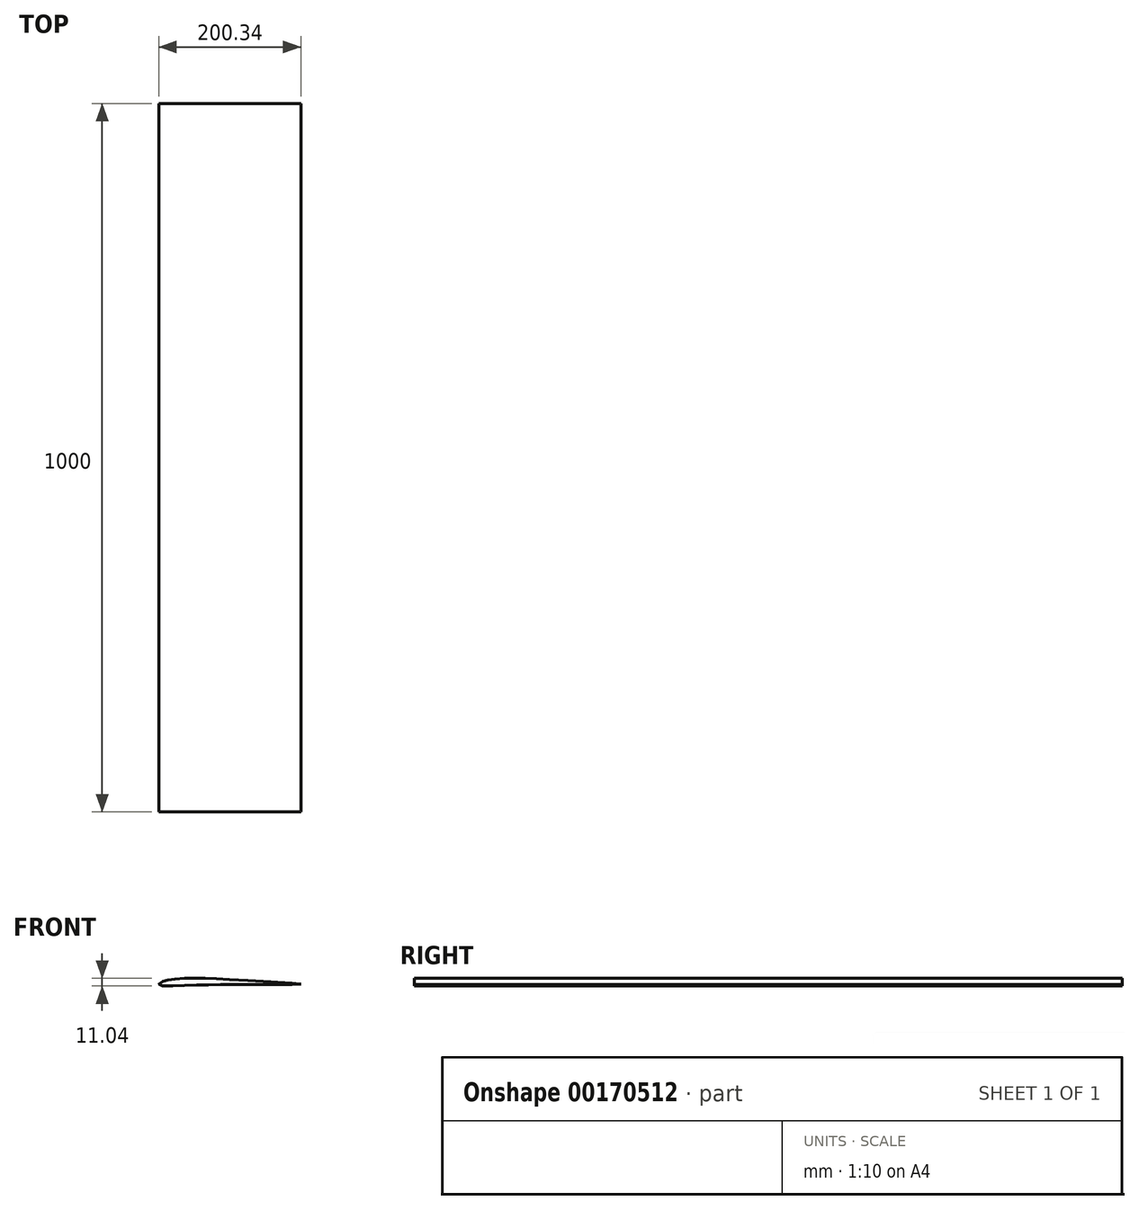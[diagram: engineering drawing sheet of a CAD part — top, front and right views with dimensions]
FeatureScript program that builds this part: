
annotation { "Feature Type Name" : "Feature", "Feature Type Description" : "" }
export const myFeature = defineFeature(function(context is Context, id is Id, definition is map)
    precondition{}
    {
        {
            var Q0;
            Q0=qCreatedBy(makeId("Front.planeOp"),FACE);
            var sketch = newSketch(context, id + "F0", { "sketchPlane" : qUnion([Q0])});
            skFitSpline(sketch, "E0", {"points": [v(100.45, -2.66) * mm, v(24.86, 2.92) * mm, v(-27.31, 5.27) * mm, v(-54.18, 5.8) * mm, v(-77.3, 4.6) * mm, v(-88.36, 2.92) * mm, v(-94.25, 1.21) * mm, v(-99.46, -1.66) * mm, v(-99.55, -3.52) * mm, v(-86.5, -5.23) * mm, v(-53.66, -4.12) * mm, v(-19.23, -3.34) * mm, v(34.77, -3.08) * mm, v(100.45, -2.66) * mm]});
            skSolve(sketch);
        }
        {
            var Q0;
            Q0 = qSketchRegion(id + "F0", true);
            extrude(context, id + "F1", {"entities" : qUnion([Q0]), "depth" : 1000 * mm});
        }
    });
